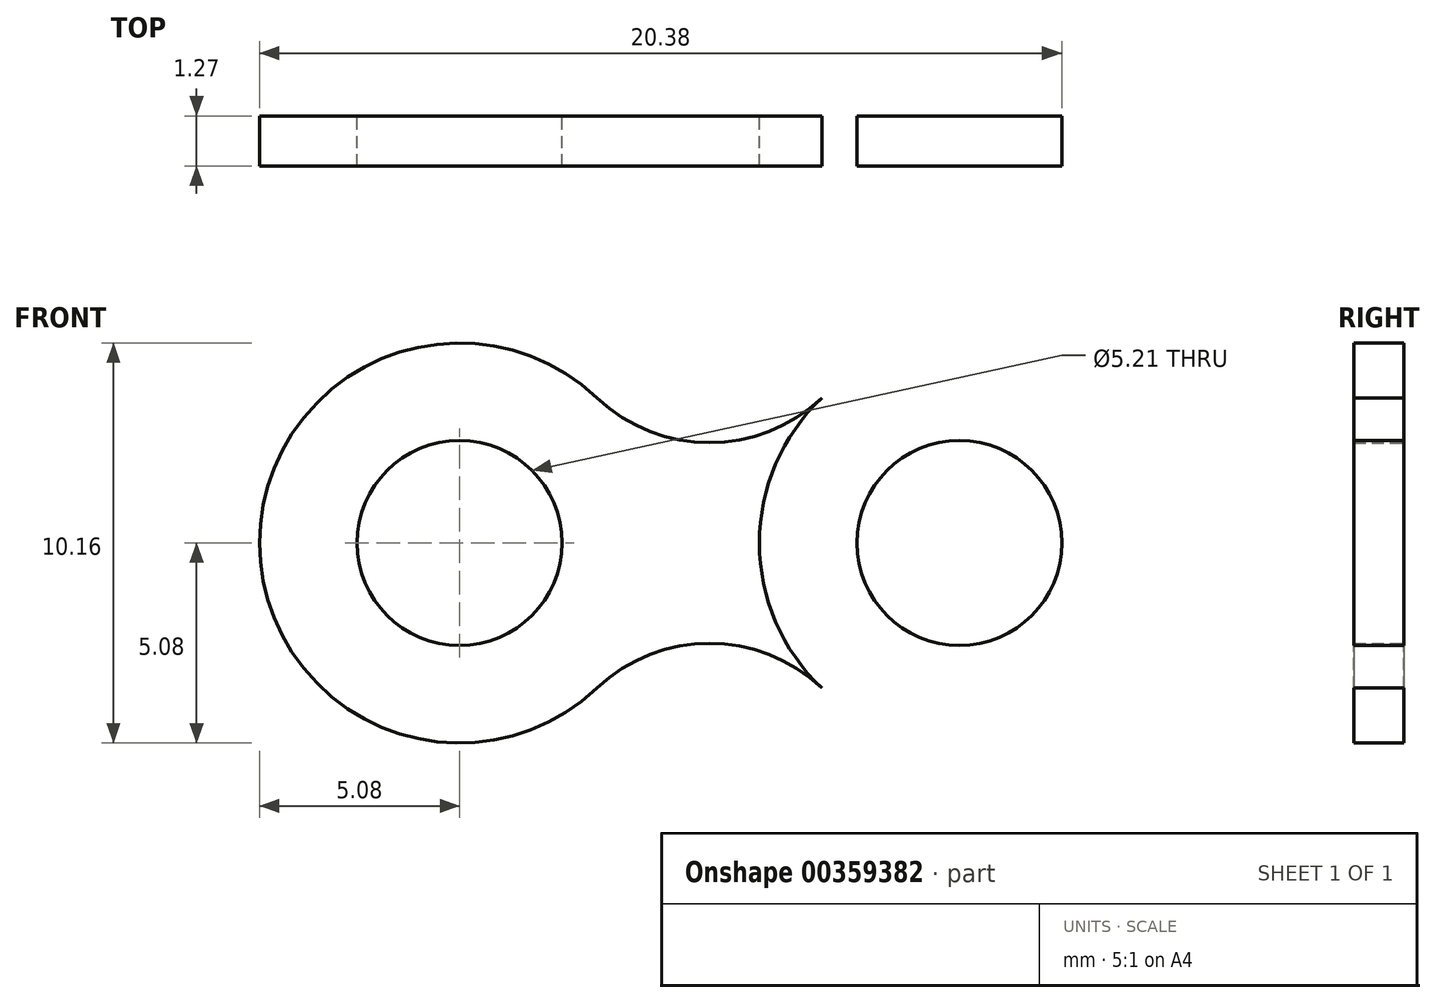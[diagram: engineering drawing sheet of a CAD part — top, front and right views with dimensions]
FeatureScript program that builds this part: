
annotation { "Feature Type Name" : "Feature", "Feature Type Description" : "" }
export const myFeature = defineFeature(function(context is Context, id is Id, definition is map)
    precondition{}
    {
        {
            var Q0;
            Q0=qCreatedBy(makeId("Front.planeOp"),FACE);
            var sketch = newSketch(context, id + "F0", { "sketchPlane" : qUnion([Q0])});
            skCircle(sketch, "E0", {"center": v(-6.35, 0) * mm, "radius": 5.08 * mm});
            skCircle(sketch, "E1", {"center": v(6.35, 0) * mm, "radius": 5.08 * mm});
            skLineSegment(sketch, "E2", {"start": v(-2.85, 3.69) * mm, "end": v(-2.85, 3.69) * mm});
            skLineSegment(sketch, "E3", {"start": v(-2.85, -3.69) * mm, "end": v(-2.85, -3.69) * mm});
            skLineSegment(sketch, "E4.MirrorCS", {"start": v(2.85, 3.69) * mm, "end": v(2.85, 3.69) * mm});
            skLineSegment(sketch, "E5.MirrorCS", {"start": v(2.85, -3.69) * mm, "end": v(2.85, -3.69) * mm});
            skArc(sketch, "E6", {"start": v(-2.85, 3.69) * mm, "mid": v(0, 2.55) * mm, "end": v(2.85, 3.69) * mm});
            skArc(sketch, "E7.MirrorCS", {"start": v(-2.85, -3.69) * mm, "mid": v(0, -2.55) * mm, "end": v(2.85, -3.69) * mm});
            skCircle(sketch, "E8", {"center": v(-6.35, 0) * mm, "radius": 2.6 * mm});
            skCircle(sketch, "E9.MirrorC", {"center": v(6.35, 0) * mm, "radius": 2.6 * mm});
            skSolve(sketch);
        }
        {
            var Q0;
            Q0=makeQuery(id+"F0.imprint","IMPRINT",FACE,{"disambiguationData":[TD([[makeQuery(id+"F0.imprint","IMPRINT",EDGE,{"derivedFrom":sQuery(id+"F0.wireOp",EDGE,"E9.MirrorC")}),1.0]])]});
            var Q1;
            Q1=makeQuery(id+"F0.imprint","IMPRINT",FACE,{"disambiguationData":[TD([[makeQuery(id+"F0.imprint","IMPRINT",EDGE,{"derivedFrom":sQuery(id+"F0.wireOp",EDGE,"E8")}),-1.0]])]});
            var Q2;
            {var subQ0=sQuery(id+"F0.wireOp",EDGE,"E6");Q2=makeQuery(id+"F0.imprint","IMPRINT",FACE,{"disambiguationData":[TD([[makeQuery(id+"F0.imprint","IMPRINT",EDGE,{"derivedFrom":subQ0}),-1.0]])]});}
            extrude(context, id + "F1", {"entities" : qUnion([Q0, Q1, Q2]), "depth" : 1.27 * mm});
        }
    });
